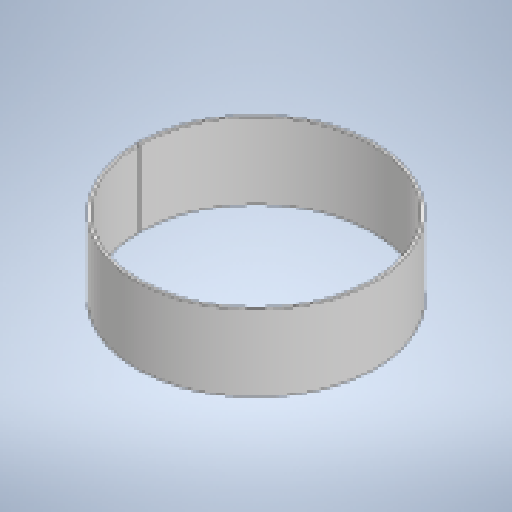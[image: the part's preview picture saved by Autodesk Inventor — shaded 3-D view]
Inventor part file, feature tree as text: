
AUTODESK INVENTOR PART (.ipt)
format: ipt  version: 2025.4 (Build 294407000, 407)  size: 183,296 bytes
history: native  units: mm
features: sketch x2, revolve x1, extrude x1, other x1
ambient origin geometry x8: Origin, YZ Plane, XZ Plane, XY Plane, X Axis, Y Axis, Z Axis, Center Point
bodies: Solid1 (feature_tree)
feature tree (5):
  revolve  "Revolution1"  [1 undecoded]
  extrude  "Extrusion1"  Depth=6.0mm
  sketch  "Sketch1"  dims[d1=6.0mm d3=6.0mm d5=120.0mm]
  sketch  "Sketch2"  dims[d6=62.8144mm d7=6.0mm d8=50.0mm d9=952.0mm d10=0.0mm d11=0.0mm d12=535.0mm]
  other  "Definition1"
note: 1 required parameter value undecoded (feature->parameter linkage not recoverable at this tier; creation-order binding heuristic only, values carry confidence <= 0.55)
